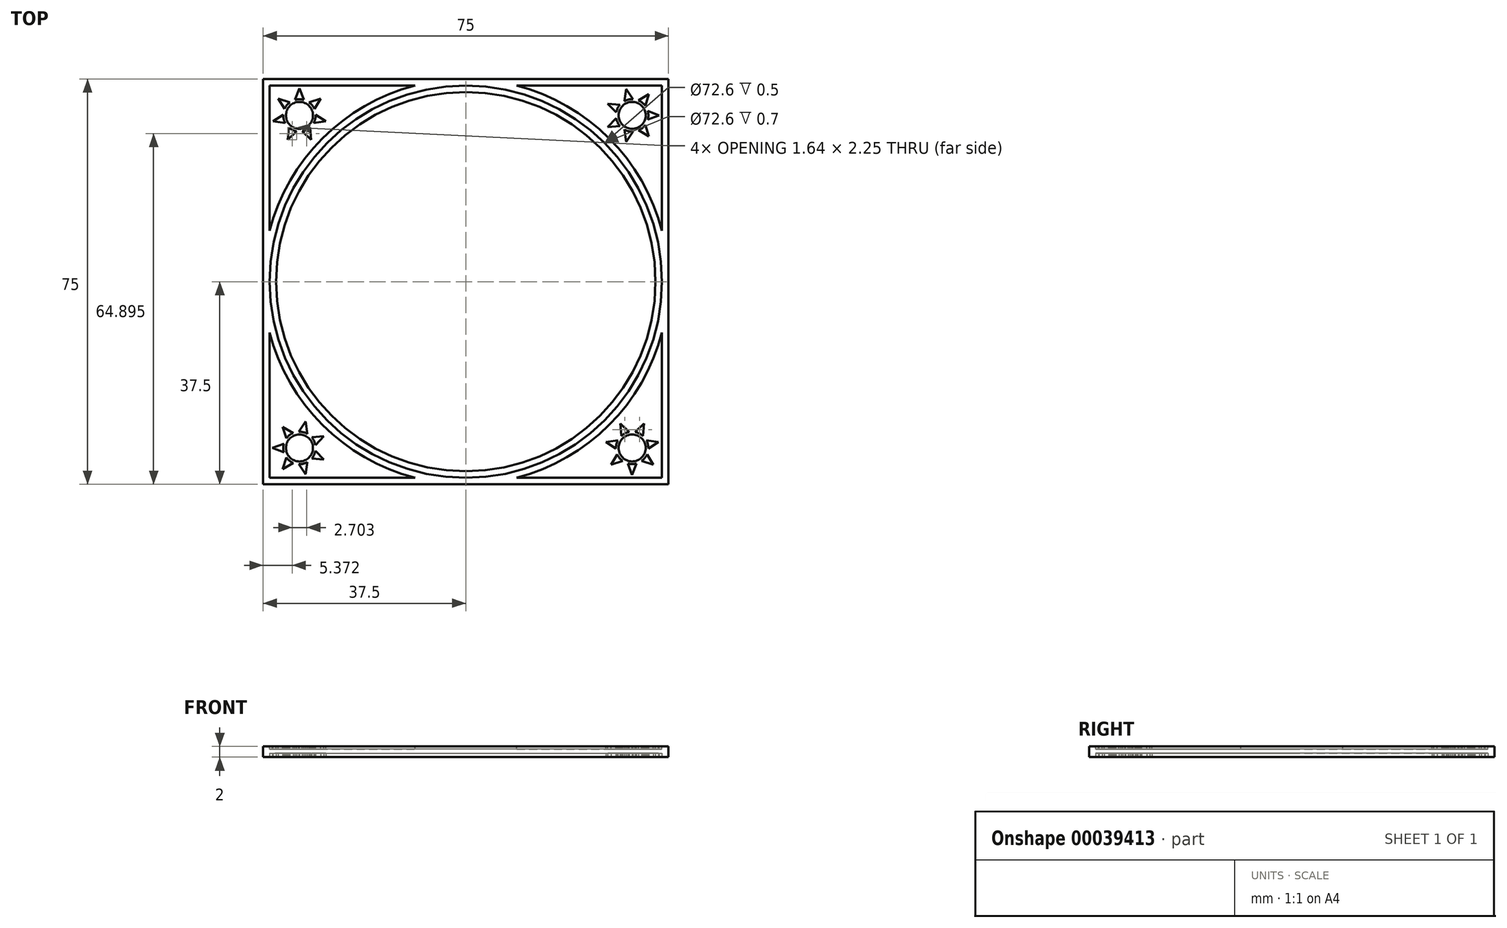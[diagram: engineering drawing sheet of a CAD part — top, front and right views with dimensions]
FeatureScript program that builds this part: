
annotation { "Feature Type Name" : "Feature", "Feature Type Description" : "" }
export const myFeature = defineFeature(function(context is Context, id is Id, definition is map)
    precondition{}
    {
        {
            var Q0;
            Q0=qCreatedBy(makeId("Top.planeOp"),FACE);
            var sketch = newSketch(context, id + "F0", { "sketchPlane" : qUnion([Q0])});
            skLineSegment(sketch, "E0.rect.bottom", {"start": v(37.5, -37.5) * mm, "end": v(-37.5, -37.5) * mm});
            skLineSegment(sketch, "E0.rect.top", {"start": v(37.5, 37.5) * mm, "end": v(-37.5, 37.5) * mm});
            skLineSegment(sketch, "E0.rect.left", {"start": v(37.5, -37.5) * mm, "end": v(37.5, 37.5) * mm});
            skLineSegment(sketch, "E0.rect.right", {"start": v(-37.5, -37.5) * mm, "end": v(-37.5, 37.5) * mm});
            skPoint(sketch, "E0.rect.middle", {"position": v(0, 0) * mm});
            skSolve(sketch);
        }
        {
            var Q0;
            Q0 = qSketchRegion(id + "F0", true);
            extrude(context, id + "F1", {"entities" : qUnion([Q0]), "depth" : 2 * mm});
        }
        {
            var Q0;
            Q0=makeQuery(id+"F1.opExtrude","CAP_FACE",FACE,{"disambiguationData":[OSD([sQuery(id+"F0.wireOp",EDGE,"E0.rect.bottom"),sQuery(id+"F0.wireOp",EDGE,"E0.rect.top"),sQuery(id+"F0.wireOp",EDGE,"E0.rect.left"),sQuery(id+"F0.wireOp",EDGE,"E0.rect.right")])],"isStart":false});
            var sketch = newSketch(context, id + "F2", { "sketchPlane" : qUnion([Q0])});
            skLineSegment(sketch, "E1.rect.bottom", {"start": v(36.3, -36.3) * mm, "end": v(9.41, -36.3) * mm});
            skLineSegment(sketch, "E1.rect.top", {"start": v(36.3, 36.3) * mm, "end": v(9.41, 36.3) * mm});
            skLineSegment(sketch, "E1.rect.left", {"start": v(36.3, -36.3) * mm, "end": v(36.3, -9.41) * mm});
            skLineSegment(sketch, "E1.rect.right", {"start": v(-36.3, -36.3) * mm, "end": v(-36.3, -9.41) * mm});
            skPoint(sketch, "E1.rect.middle", {"position": v(0, 0) * mm});
            skCircle(sketch, "E2", {"center": v(0, 0) * mm, "radius": 35.1 * mm});
            skArc(sketch, "E3", {"start": v(-9.41, 36.3) * mm, "mid": v(-26.52, 26.52) * mm, "end": v(-36.3, 9.41) * mm});
            skArc(sketch, "E4.trimOffspring", {"start": v(36.3, 9.41) * mm, "mid": v(26.52, 26.52) * mm, "end": v(9.41, 36.3) * mm});
            skArc(sketch, "E5.trimOffspring", {"start": v(9.41, -36.3) * mm, "mid": v(26.52, -26.52) * mm, "end": v(36.3, -9.41) * mm});
            skArc(sketch, "E6.trimOffspring", {"start": v(-36.3, -9.41) * mm, "mid": v(-26.52, -26.52) * mm, "end": v(-9.41, -36.3) * mm});
            skLineSegment(sketch, "E7.trimOffspring", {"start": v(-36.3, 9.41) * mm, "end": v(-36.3, 36.3) * mm});
            skLineSegment(sketch, "E8.trimOffspring", {"start": v(-9.41, 36.3) * mm, "end": v(-36.3, 36.3) * mm});
            skLineSegment(sketch, "E9.trimOffspring", {"start": v(36.3, 9.41) * mm, "end": v(36.3, 36.3) * mm});
            skLineSegment(sketch, "E10.trimOffspring", {"start": v(-9.41, -36.3) * mm, "end": v(-36.3, -36.3) * mm});
            skCircle(sketch, "E11", {"center": v(0, 0) * mm, "radius": 36.3 * mm});
            skLineSegment(sketch, "E12", {"start": v(-36.3, 36.3) * mm, "end": v(-26.52, 26.52) * mm, "construction": true});
            skCircle(sketch, "E13", {"center": v(-30.78, 30.78) * mm, "radius": 2.5 * mm});
            skArc(sketch, "E14", {"start": v(-29.98, 33.67) * mm, "mid": v(-30.78, 33.78) * mm, "end": v(-31.58, 33.67) * mm});
            skLineSegment(sketch, "E15", {"start": v(-31.58, 33.67) * mm, "end": v(-30.78, 35.78) * mm});
            skLineSegment(sketch, "E16", {"start": v(-30.78, 35.78) * mm, "end": v(-29.98, 33.67) * mm});
            skArc(sketch, "E17.1.0", {"start": v(-32.54, 33.2) * mm, "mid": v(-33.12, 32.65) * mm, "end": v(-33.54, 31.95) * mm});
            skLineSegment(sketch, "E17.1.1", {"start": v(-34.69, 33.9) * mm, "end": v(-32.54, 33.2) * mm});
            skLineSegment(sketch, "E17.1.2", {"start": v(-33.54, 31.95) * mm, "end": v(-34.69, 33.9) * mm});
            skArc(sketch, "E17.2.0", {"start": v(-33.77, 30.91) * mm, "mid": v(-33.7, 30.1) * mm, "end": v(-33.42, 29.35) * mm});
            skLineSegment(sketch, "E17.2.1", {"start": v(-35.65, 29.66) * mm, "end": v(-33.77, 30.91) * mm});
            skLineSegment(sketch, "E17.2.2", {"start": v(-33.42, 29.35) * mm, "end": v(-35.65, 29.66) * mm});
            skArc(sketch, "E18.1.3.0", {"start": v(-32.75, 28.52) * mm, "mid": v(-32.08, 28.07) * mm, "end": v(-31.31, 27.82) * mm});
            skLineSegment(sketch, "E18.4.3.0", {"start": v(-32.95, 26.27) * mm, "end": v(-32.75, 28.52) * mm});
            skLineSegment(sketch, "E18.7.3.0", {"start": v(-31.31, 27.82) * mm, "end": v(-32.95, 26.27) * mm});
            skArc(sketch, "E18.1.4.0", {"start": v(-30.24, 27.82) * mm, "mid": v(-29.47, 28.07) * mm, "end": v(-28.8, 28.52) * mm});
            skLineSegment(sketch, "E18.4.4.0", {"start": v(-28.6, 26.27) * mm, "end": v(-30.24, 27.82) * mm});
            skLineSegment(sketch, "E18.7.4.0", {"start": v(-28.8, 28.52) * mm, "end": v(-28.6, 26.27) * mm});
            skArc(sketch, "E18.1.5.0", {"start": v(-28.14, 29.35) * mm, "mid": v(-27.85, 30.1) * mm, "end": v(-27.78, 30.91) * mm});
            skLineSegment(sketch, "E18.4.5.0", {"start": v(-25.9, 29.66) * mm, "end": v(-28.14, 29.35) * mm});
            skLineSegment(sketch, "E18.7.5.0", {"start": v(-27.78, 30.91) * mm, "end": v(-25.9, 29.66) * mm});
            skArc(sketch, "E18.1.6.0", {"start": v(-28.02, 31.95) * mm, "mid": v(-28.43, 32.65) * mm, "end": v(-29.01, 33.2) * mm});
            skLineSegment(sketch, "E18.4.6.0", {"start": v(-26.87, 33.9) * mm, "end": v(-28.02, 31.95) * mm});
            skLineSegment(sketch, "E18.7.6.0", {"start": v(-29.01, 33.2) * mm, "end": v(-26.87, 33.9) * mm});
            skCircle(sketch, "E19.1.0", {"center": v(-30.78, -30.78) * mm, "radius": 2.5 * mm});
            skArc(sketch, "E19.1.1", {"start": v(-33.67, -29.98) * mm, "mid": v(-33.78, -30.78) * mm, "end": v(-33.67, -31.58) * mm});
            skLineSegment(sketch, "E19.1.2", {"start": v(-33.67, -31.58) * mm, "end": v(-35.78, -30.78) * mm});
            skLineSegment(sketch, "E19.1.3", {"start": v(-35.78, -30.78) * mm, "end": v(-33.67, -29.98) * mm});
            skLineSegment(sketch, "E19.1.4", {"start": v(-33.2, -29.01) * mm, "end": v(-33.9, -26.87) * mm});
            skArc(sketch, "E19.1.5", {"start": v(-31.95, -28.02) * mm, "mid": v(-32.65, -28.43) * mm, "end": v(-33.2, -29.01) * mm});
            skLineSegment(sketch, "E19.1.6", {"start": v(-33.9, -26.87) * mm, "end": v(-31.95, -28.02) * mm});
            skLineSegment(sketch, "E19.1.7", {"start": v(-30.91, -27.78) * mm, "end": v(-29.66, -25.9) * mm});
            skArc(sketch, "E19.1.8", {"start": v(-29.35, -28.14) * mm, "mid": v(-30.1, -27.85) * mm, "end": v(-30.91, -27.78) * mm});
            skLineSegment(sketch, "E19.1.9", {"start": v(-29.66, -25.9) * mm, "end": v(-29.35, -28.14) * mm});
            skLineSegment(sketch, "E19.1.10", {"start": v(-28.52, -28.8) * mm, "end": v(-26.27, -28.6) * mm});
            skArc(sketch, "E19.1.11", {"start": v(-27.82, -30.24) * mm, "mid": v(-28.07, -29.47) * mm, "end": v(-28.52, -28.8) * mm});
            skLineSegment(sketch, "E19.1.12", {"start": v(-26.27, -28.6) * mm, "end": v(-27.82, -30.24) * mm});
            skLineSegment(sketch, "E19.1.13", {"start": v(-27.82, -31.31) * mm, "end": v(-26.27, -32.95) * mm});
            skArc(sketch, "E19.1.14", {"start": v(-28.52, -32.75) * mm, "mid": v(-28.07, -32.08) * mm, "end": v(-27.82, -31.31) * mm});
            skLineSegment(sketch, "E19.1.15", {"start": v(-26.27, -32.95) * mm, "end": v(-28.52, -32.75) * mm});
            skLineSegment(sketch, "E19.1.16", {"start": v(-29.35, -33.42) * mm, "end": v(-29.66, -35.65) * mm});
            skLineSegment(sketch, "E19.1.17", {"start": v(-29.66, -35.65) * mm, "end": v(-30.91, -33.77) * mm});
            skArc(sketch, "E19.1.18", {"start": v(-30.91, -33.77) * mm, "mid": v(-30.1, -33.7) * mm, "end": v(-29.35, -33.42) * mm});
            skLineSegment(sketch, "E19.1.19", {"start": v(-31.95, -33.54) * mm, "end": v(-33.9, -34.69) * mm});
            skLineSegment(sketch, "E19.1.20", {"start": v(-33.9, -34.69) * mm, "end": v(-33.2, -32.54) * mm});
            skArc(sketch, "E19.1.21", {"start": v(-33.2, -32.54) * mm, "mid": v(-32.65, -33.12) * mm, "end": v(-31.95, -33.54) * mm});
            skCircle(sketch, "E19.2.0", {"center": v(30.78, -30.78) * mm, "radius": 2.5 * mm});
            skArc(sketch, "E19.2.1", {"start": v(29.98, -33.67) * mm, "mid": v(30.78, -33.78) * mm, "end": v(31.58, -33.67) * mm});
            skLineSegment(sketch, "E19.2.2", {"start": v(31.58, -33.67) * mm, "end": v(30.78, -35.78) * mm});
            skLineSegment(sketch, "E19.2.3", {"start": v(30.78, -35.78) * mm, "end": v(29.98, -33.67) * mm});
            skLineSegment(sketch, "E19.2.4", {"start": v(29.01, -33.2) * mm, "end": v(26.87, -33.9) * mm});
            skArc(sketch, "E19.2.5", {"start": v(28.02, -31.95) * mm, "mid": v(28.43, -32.65) * mm, "end": v(29.01, -33.2) * mm});
            skLineSegment(sketch, "E19.2.6", {"start": v(26.87, -33.9) * mm, "end": v(28.02, -31.95) * mm});
            skLineSegment(sketch, "E19.2.7", {"start": v(27.78, -30.91) * mm, "end": v(25.9, -29.66) * mm});
            skArc(sketch, "E19.2.8", {"start": v(28.14, -29.35) * mm, "mid": v(27.85, -30.1) * mm, "end": v(27.78, -30.91) * mm});
            skLineSegment(sketch, "E19.2.9", {"start": v(25.9, -29.66) * mm, "end": v(28.14, -29.35) * mm});
            skLineSegment(sketch, "E19.2.10", {"start": v(28.8, -28.52) * mm, "end": v(28.6, -26.27) * mm});
            skArc(sketch, "E19.2.11", {"start": v(30.24, -27.82) * mm, "mid": v(29.47, -28.07) * mm, "end": v(28.8, -28.52) * mm});
            skLineSegment(sketch, "E19.2.12", {"start": v(28.6, -26.27) * mm, "end": v(30.24, -27.82) * mm});
            skLineSegment(sketch, "E19.2.13", {"start": v(31.31, -27.82) * mm, "end": v(32.95, -26.27) * mm});
            skArc(sketch, "E19.2.14", {"start": v(32.75, -28.52) * mm, "mid": v(32.08, -28.07) * mm, "end": v(31.31, -27.82) * mm});
            skLineSegment(sketch, "E19.2.15", {"start": v(32.95, -26.27) * mm, "end": v(32.75, -28.52) * mm});
            skLineSegment(sketch, "E19.2.16", {"start": v(33.42, -29.35) * mm, "end": v(35.65, -29.66) * mm});
            skLineSegment(sketch, "E19.2.17", {"start": v(35.65, -29.66) * mm, "end": v(33.77, -30.91) * mm});
            skArc(sketch, "E19.2.18", {"start": v(33.77, -30.91) * mm, "mid": v(33.7, -30.1) * mm, "end": v(33.42, -29.35) * mm});
            skLineSegment(sketch, "E19.2.19", {"start": v(33.54, -31.95) * mm, "end": v(34.69, -33.9) * mm});
            skLineSegment(sketch, "E19.2.20", {"start": v(34.69, -33.9) * mm, "end": v(32.54, -33.2) * mm});
            skArc(sketch, "E19.2.21", {"start": v(32.54, -33.2) * mm, "mid": v(33.12, -32.65) * mm, "end": v(33.54, -31.95) * mm});
            skCircle(sketch, "E20.1.3.0", {"center": v(30.78, 30.78) * mm, "radius": 2.5 * mm});
            skArc(sketch, "E20.2.3.0", {"start": v(33.67, 29.98) * mm, "mid": v(33.78, 30.78) * mm, "end": v(33.67, 31.58) * mm});
            skLineSegment(sketch, "E20.6.3.0", {"start": v(33.67, 31.58) * mm, "end": v(35.78, 30.78) * mm});
            skLineSegment(sketch, "E20.9.3.0", {"start": v(35.78, 30.78) * mm, "end": v(33.67, 29.98) * mm});
            skLineSegment(sketch, "E20.12.3.0", {"start": v(33.2, 29.01) * mm, "end": v(33.9, 26.87) * mm});
            skArc(sketch, "E20.15.3.0", {"start": v(31.95, 28.02) * mm, "mid": v(32.65, 28.43) * mm, "end": v(33.2, 29.01) * mm});
            skLineSegment(sketch, "E20.19.3.0", {"start": v(33.9, 26.87) * mm, "end": v(31.95, 28.02) * mm});
            skLineSegment(sketch, "E20.22.3.0", {"start": v(30.91, 27.78) * mm, "end": v(29.66, 25.9) * mm});
            skArc(sketch, "E20.25.3.0", {"start": v(29.35, 28.14) * mm, "mid": v(30.1, 27.85) * mm, "end": v(30.91, 27.78) * mm});
            skLineSegment(sketch, "E20.29.3.0", {"start": v(29.66, 25.9) * mm, "end": v(29.35, 28.14) * mm});
            skLineSegment(sketch, "E20.32.3.0", {"start": v(28.52, 28.8) * mm, "end": v(26.27, 28.6) * mm});
            skArc(sketch, "E20.35.3.0", {"start": v(27.82, 30.24) * mm, "mid": v(28.07, 29.47) * mm, "end": v(28.52, 28.8) * mm});
            skLineSegment(sketch, "E20.39.3.0", {"start": v(26.27, 28.6) * mm, "end": v(27.82, 30.24) * mm});
            skLineSegment(sketch, "E20.42.3.0", {"start": v(27.82, 31.31) * mm, "end": v(26.27, 32.95) * mm});
            skArc(sketch, "E20.45.3.0", {"start": v(28.52, 32.75) * mm, "mid": v(28.07, 32.08) * mm, "end": v(27.82, 31.31) * mm});
            skLineSegment(sketch, "E20.49.3.0", {"start": v(26.27, 32.95) * mm, "end": v(28.52, 32.75) * mm});
            skLineSegment(sketch, "E20.52.3.0", {"start": v(29.35, 33.42) * mm, "end": v(29.66, 35.65) * mm});
            skLineSegment(sketch, "E20.55.3.0", {"start": v(29.66, 35.65) * mm, "end": v(30.91, 33.77) * mm});
            skArc(sketch, "E20.58.3.0", {"start": v(30.91, 33.77) * mm, "mid": v(30.1, 33.7) * mm, "end": v(29.35, 33.42) * mm});
            skLineSegment(sketch, "E20.62.3.0", {"start": v(31.95, 33.54) * mm, "end": v(33.9, 34.69) * mm});
            skLineSegment(sketch, "E20.65.3.0", {"start": v(33.9, 34.69) * mm, "end": v(33.2, 32.54) * mm});
            skArc(sketch, "E20.68.3.0", {"start": v(33.2, 32.54) * mm, "mid": v(32.65, 33.12) * mm, "end": v(31.95, 33.54) * mm});
            skSolve(sketch);
        }
        {
            var Q0;
            Q0 = qSketchRegion(id + "F2", true);
            extrude(context, id + "F3", {"entities" : qUnion([Q0]), "operationType" : NewBodyOperationType.REMOVE, "oppositeDirection" : true, "depth" : 0.5 * mm});
        }
        {
            var Q0;
            Q0=makeQuery(id+"F1.opExtrude","CAP_FACE",FACE,{"disambiguationData":[OSD([sQuery(id+"F0.wireOp",EDGE,"E0.rect.bottom"),sQuery(id+"F0.wireOp",EDGE,"E0.rect.top"),sQuery(id+"F0.wireOp",EDGE,"E0.rect.left"),sQuery(id+"F0.wireOp",EDGE,"E0.rect.right")])],"isStart":true});
            var sketch = newSketch(context, id + "F4", { "sketchPlane" : qUnion([Q0])});
            skLineSegment(sketch, "E21.0.0", {"start": v(29.98, 33.67) * mm, "end": v(30.78, 35.78) * mm});
            skLineSegment(sketch, "E21.0.1", {"start": v(30.78, 35.78) * mm, "end": v(31.58, 33.67) * mm});
            skArc(sketch, "E21.0.2", {"start": v(31.58, 33.67) * mm, "mid": v(30.78, 33.78) * mm, "end": v(29.98, 33.67) * mm});
            skArc(sketch, "E22.0.0", {"start": v(29.01, 33.2) * mm, "mid": v(28.43, 32.65) * mm, "end": v(28.02, 31.95) * mm});
            skLineSegment(sketch, "E22.0.1", {"start": v(28.02, 31.95) * mm, "end": v(26.87, 33.9) * mm});
            skLineSegment(sketch, "E22.0.2", {"start": v(26.87, 33.9) * mm, "end": v(29.01, 33.2) * mm});
            skArc(sketch, "E23.0.0", {"start": v(27.78, 30.91) * mm, "mid": v(27.85, 30.1) * mm, "end": v(28.14, 29.35) * mm});
            skLineSegment(sketch, "E23.0.1", {"start": v(28.14, 29.35) * mm, "end": v(25.9, 29.66) * mm});
            skLineSegment(sketch, "E23.0.2", {"start": v(25.9, 29.66) * mm, "end": v(27.78, 30.91) * mm});
            skArc(sketch, "E24.0.0", {"start": v(28.8, 28.52) * mm, "mid": v(29.47, 28.07) * mm, "end": v(30.24, 27.82) * mm});
            skLineSegment(sketch, "E24.0.1", {"start": v(30.24, 27.82) * mm, "end": v(28.6, 26.27) * mm});
            skLineSegment(sketch, "E24.0.2", {"start": v(28.6, 26.27) * mm, "end": v(28.8, 28.52) * mm});
            skArc(sketch, "E25.0.0", {"start": v(31.31, 27.82) * mm, "mid": v(32.08, 28.07) * mm, "end": v(32.75, 28.52) * mm});
            skLineSegment(sketch, "E25.0.1", {"start": v(32.75, 28.52) * mm, "end": v(32.95, 26.27) * mm});
            skLineSegment(sketch, "E25.0.2", {"start": v(32.95, 26.27) * mm, "end": v(31.31, 27.82) * mm});
            skArc(sketch, "E26.0.0", {"start": v(33.42, 29.35) * mm, "mid": v(33.7, 30.1) * mm, "end": v(33.77, 30.91) * mm});
            skLineSegment(sketch, "E26.0.1", {"start": v(33.77, 30.91) * mm, "end": v(35.65, 29.66) * mm});
            skLineSegment(sketch, "E26.0.2", {"start": v(35.65, 29.66) * mm, "end": v(33.42, 29.35) * mm});
            skArc(sketch, "E27.0.0", {"start": v(33.54, 31.95) * mm, "mid": v(33.12, 32.65) * mm, "end": v(32.54, 33.2) * mm});
            skLineSegment(sketch, "E27.0.1", {"start": v(32.54, 33.2) * mm, "end": v(34.69, 33.9) * mm});
            skLineSegment(sketch, "E27.0.2", {"start": v(34.69, 33.9) * mm, "end": v(33.54, 31.95) * mm});
            skArc(sketch, "E28.0.0", {"start": v(-29.35, 33.42) * mm, "mid": v(-30.1, 33.7) * mm, "end": v(-30.91, 33.77) * mm});
            skLineSegment(sketch, "E28.0.1", {"start": v(-30.91, 33.77) * mm, "end": v(-29.66, 35.65) * mm});
            skLineSegment(sketch, "E28.0.2", {"start": v(-29.66, 35.65) * mm, "end": v(-29.35, 33.42) * mm});
            skArc(sketch, "E29.0.0", {"start": v(-31.95, 33.54) * mm, "mid": v(-32.65, 33.12) * mm, "end": v(-33.2, 32.54) * mm});
            skLineSegment(sketch, "E29.0.1", {"start": v(-33.2, 32.54) * mm, "end": v(-33.9, 34.69) * mm});
            skLineSegment(sketch, "E29.0.2", {"start": v(-33.9, 34.69) * mm, "end": v(-31.95, 33.54) * mm});
            skLineSegment(sketch, "E30.0.0", {"start": v(-33.67, 29.98) * mm, "end": v(-35.78, 30.78) * mm});
            skLineSegment(sketch, "E30.0.1", {"start": v(-35.78, 30.78) * mm, "end": v(-33.67, 31.58) * mm});
            skArc(sketch, "E30.0.2", {"start": v(-33.67, 31.58) * mm, "mid": v(-33.78, 30.78) * mm, "end": v(-33.67, 29.98) * mm});
            skLineSegment(sketch, "E31.0", {"start": v(-33.9, 26.87) * mm, "end": v(-31.95, 28.02) * mm});
            skArc(sketch, "E32.0.0", {"start": v(-33.2, 29.01) * mm, "mid": v(-32.65, 28.43) * mm, "end": v(-31.95, 28.02) * mm});
            skLineSegment(sketch, "E32.0.1", {"start": v(-31.95, 28.02) * mm, "end": v(-33.9, 26.87) * mm});
            skLineSegment(sketch, "E32.0.2", {"start": v(-33.9, 26.87) * mm, "end": v(-33.2, 29.01) * mm});
            skArc(sketch, "E33.0.0", {"start": v(-30.91, 27.78) * mm, "mid": v(-30.1, 27.85) * mm, "end": v(-29.35, 28.14) * mm});
            skLineSegment(sketch, "E33.0.1", {"start": v(-29.35, 28.14) * mm, "end": v(-29.66, 25.9) * mm});
            skLineSegment(sketch, "E33.0.2", {"start": v(-29.66, 25.9) * mm, "end": v(-30.91, 27.78) * mm});
            skArc(sketch, "E34.0.0", {"start": v(-28.52, 28.8) * mm, "mid": v(-28.07, 29.47) * mm, "end": v(-27.82, 30.24) * mm});
            skLineSegment(sketch, "E34.0.1", {"start": v(-27.82, 30.24) * mm, "end": v(-26.27, 28.6) * mm});
            skLineSegment(sketch, "E34.0.2", {"start": v(-26.27, 28.6) * mm, "end": v(-28.52, 28.8) * mm});
            skArc(sketch, "E35.0.0", {"start": v(-27.82, 31.31) * mm, "mid": v(-28.07, 32.08) * mm, "end": v(-28.52, 32.75) * mm});
            skLineSegment(sketch, "E35.0.1", {"start": v(-28.52, 32.75) * mm, "end": v(-26.27, 32.95) * mm});
            skLineSegment(sketch, "E35.0.2", {"start": v(-26.27, 32.95) * mm, "end": v(-27.82, 31.31) * mm});
            skLineSegment(sketch, "E36.0.0", {"start": v(-30.24, -27.82) * mm, "end": v(-28.6, -26.27) * mm});
            skLineSegment(sketch, "E36.0.1", {"start": v(-28.6, -26.27) * mm, "end": v(-28.8, -28.52) * mm});
            skArc(sketch, "E36.0.2", {"start": v(-28.8, -28.52) * mm, "mid": v(-29.47, -28.07) * mm, "end": v(-30.24, -27.82) * mm});
            skLineSegment(sketch, "E37.0.0", {"start": v(-32.75, -28.52) * mm, "end": v(-32.95, -26.27) * mm});
            skLineSegment(sketch, "E37.0.1", {"start": v(-32.95, -26.27) * mm, "end": v(-31.31, -27.82) * mm});
            skArc(sketch, "E37.0.2", {"start": v(-31.31, -27.82) * mm, "mid": v(-32.08, -28.07) * mm, "end": v(-32.75, -28.52) * mm});
            skLineSegment(sketch, "E38.0.0", {"start": v(-33.77, -30.91) * mm, "end": v(-35.65, -29.66) * mm});
            skLineSegment(sketch, "E38.0.1", {"start": v(-35.65, -29.66) * mm, "end": v(-33.42, -29.35) * mm});
            skArc(sketch, "E38.0.2", {"start": v(-33.42, -29.35) * mm, "mid": v(-33.7, -30.1) * mm, "end": v(-33.77, -30.91) * mm});
            skLineSegment(sketch, "E39.0.0", {"start": v(-32.54, -33.2) * mm, "end": v(-34.69, -33.9) * mm});
            skLineSegment(sketch, "E39.0.1", {"start": v(-34.69, -33.9) * mm, "end": v(-33.54, -31.95) * mm});
            skArc(sketch, "E39.0.2", {"start": v(-33.54, -31.95) * mm, "mid": v(-33.12, -32.65) * mm, "end": v(-32.54, -33.2) * mm});
            skLineSegment(sketch, "E40.0.0", {"start": v(-29.98, -33.67) * mm, "end": v(-30.78, -35.78) * mm});
            skLineSegment(sketch, "E40.0.1", {"start": v(-30.78, -35.78) * mm, "end": v(-31.58, -33.67) * mm});
            skArc(sketch, "E40.0.2", {"start": v(-31.58, -33.67) * mm, "mid": v(-30.78, -33.78) * mm, "end": v(-29.98, -33.67) * mm});
            skLineSegment(sketch, "E41.0.0", {"start": v(-28.02, -31.95) * mm, "end": v(-26.87, -33.9) * mm});
            skLineSegment(sketch, "E41.0.1", {"start": v(-26.87, -33.9) * mm, "end": v(-29.01, -33.2) * mm});
            skArc(sketch, "E41.0.2", {"start": v(-29.01, -33.2) * mm, "mid": v(-28.43, -32.65) * mm, "end": v(-28.02, -31.95) * mm});
            skLineSegment(sketch, "E42.0.0", {"start": v(-28.14, -29.35) * mm, "end": v(-25.9, -29.66) * mm});
            skLineSegment(sketch, "E42.0.1", {"start": v(-25.9, -29.66) * mm, "end": v(-27.78, -30.91) * mm});
            skArc(sketch, "E42.0.2", {"start": v(-27.78, -30.91) * mm, "mid": v(-27.85, -30.1) * mm, "end": v(-28.14, -29.35) * mm});
            skArc(sketch, "E43.0.0", {"start": v(30.91, -27.78) * mm, "mid": v(30.1, -27.85) * mm, "end": v(29.35, -28.14) * mm});
            skLineSegment(sketch, "E43.0.1", {"start": v(29.35, -28.14) * mm, "end": v(29.66, -25.9) * mm});
            skLineSegment(sketch, "E43.0.2", {"start": v(29.66, -25.9) * mm, "end": v(30.91, -27.78) * mm});
            skArc(sketch, "E44.0.0", {"start": v(28.52, -28.8) * mm, "mid": v(28.07, -29.47) * mm, "end": v(27.82, -30.24) * mm});
            skLineSegment(sketch, "E44.0.1", {"start": v(27.82, -30.24) * mm, "end": v(26.27, -28.6) * mm});
            skLineSegment(sketch, "E44.0.2", {"start": v(26.27, -28.6) * mm, "end": v(28.52, -28.8) * mm});
            skArc(sketch, "E45.0.0", {"start": v(27.82, -31.31) * mm, "mid": v(28.07, -32.08) * mm, "end": v(28.52, -32.75) * mm});
            skLineSegment(sketch, "E45.0.1", {"start": v(28.52, -32.75) * mm, "end": v(26.27, -32.95) * mm});
            skLineSegment(sketch, "E45.0.2", {"start": v(26.27, -32.95) * mm, "end": v(27.82, -31.31) * mm});
            skArc(sketch, "E46.0.0", {"start": v(29.35, -33.42) * mm, "mid": v(30.1, -33.7) * mm, "end": v(30.91, -33.77) * mm});
            skLineSegment(sketch, "E46.0.1", {"start": v(30.91, -33.77) * mm, "end": v(29.66, -35.65) * mm});
            skLineSegment(sketch, "E46.0.2", {"start": v(29.66, -35.65) * mm, "end": v(29.35, -33.42) * mm});
            skArc(sketch, "E47.0.0", {"start": v(31.95, -33.54) * mm, "mid": v(32.65, -33.12) * mm, "end": v(33.2, -32.54) * mm});
            skLineSegment(sketch, "E47.0.1", {"start": v(33.2, -32.54) * mm, "end": v(33.9, -34.69) * mm});
            skLineSegment(sketch, "E47.0.2", {"start": v(33.9, -34.69) * mm, "end": v(31.95, -33.54) * mm});
            skLineSegment(sketch, "E48.0.0", {"start": v(33.67, -29.98) * mm, "end": v(35.78, -30.78) * mm});
            skLineSegment(sketch, "E48.0.1", {"start": v(35.78, -30.78) * mm, "end": v(33.67, -31.58) * mm});
            skArc(sketch, "E48.0.2", {"start": v(33.67, -31.58) * mm, "mid": v(33.78, -30.78) * mm, "end": v(33.67, -29.98) * mm});
            skArc(sketch, "E49.0.0", {"start": v(33.2, -29.01) * mm, "mid": v(32.65, -28.43) * mm, "end": v(31.95, -28.02) * mm});
            skLineSegment(sketch, "E49.0.1", {"start": v(31.95, -28.02) * mm, "end": v(33.9, -26.87) * mm});
            skLineSegment(sketch, "E49.0.2", {"start": v(33.9, -26.87) * mm, "end": v(33.2, -29.01) * mm});
            skCircle(sketch, "E50.0.0", {"center": v(0, 0) * mm, "radius": 36.3 * mm});
            skCircle(sketch, "E51.0.0", {"center": v(0, 0) * mm, "radius": 35.1 * mm});
            skSolve(sketch);
        }
        {
            var Q0;
            Q0 = qSketchRegion(id + "F4", true);
            extrude(context, id + "F5", {"entities" : qUnion([Q0]), "operationType" : NewBodyOperationType.REMOVE, "oppositeDirection" : true, "depth" : .7 * mm});
        }
    });
